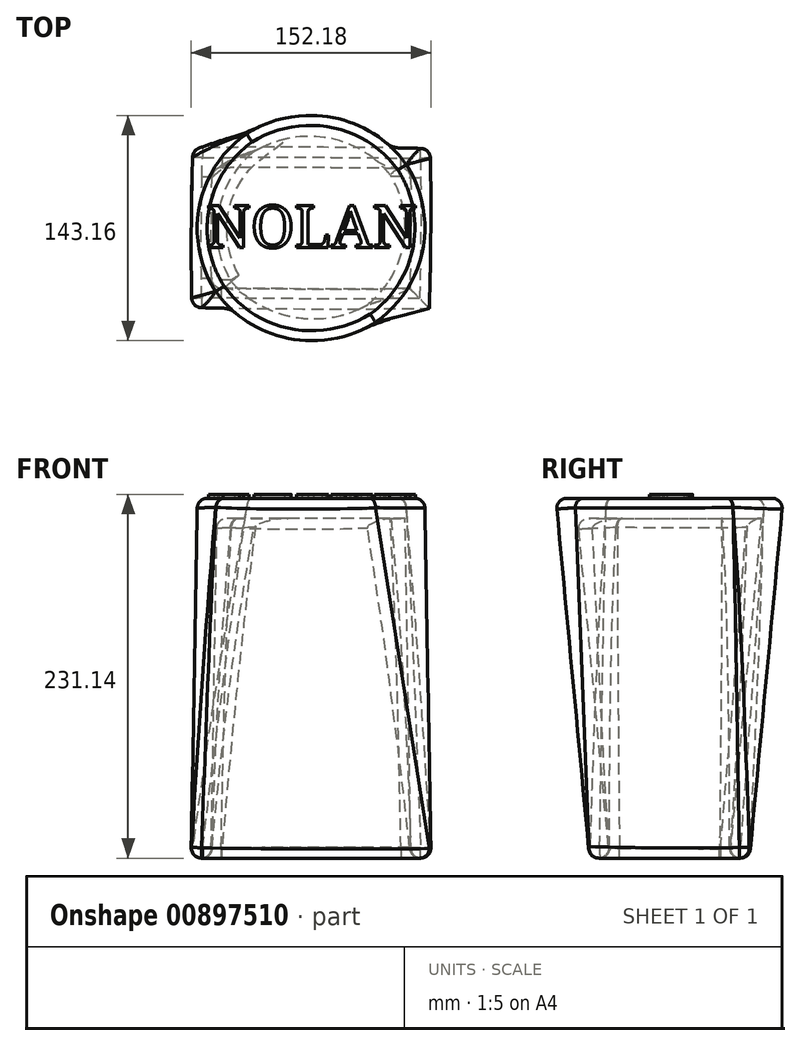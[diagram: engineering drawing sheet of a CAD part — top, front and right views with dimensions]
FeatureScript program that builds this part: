
annotation { "Feature Type Name" : "Feature", "Feature Type Description" : "" }
export const myFeature = defineFeature(function(context is Context, id is Id, definition is map)
    precondition{}
    {
        {
            var Q0;
            Q0=qCreatedBy(makeId("Top.planeOp"),FACE);
            var sketch = newSketch(context, id + "F0", { "sketchPlane" : qUnion([Q0])});
            skLineSegment(sketch, "E0.bottom", {"start": v(-76.2, -50.8) * mm, "end": v(76.2, -50.8) * mm});
            skLineSegment(sketch, "E0.top", {"start": v(-76.2, 50.8) * mm, "end": v(76.2, 50.8) * mm});
            skLineSegment(sketch, "E0.left", {"start": v(-76.2, -50.8) * mm, "end": v(-76.2, 50.8) * mm});
            skLineSegment(sketch, "E0.right", {"start": v(76.2, -50.8) * mm, "end": v(76.2, 50.8) * mm});
            skPoint(sketch, "E0.middle", {"position": v(0, 0) * mm});
            skSolve(sketch);
        }
        {
            var Q0;
            Q0=qCreatedBy(makeId("Top.planeOp"),FACE);
            cPlane(context, id + "F1", {"entities" : qUnion([Q0]), "cplaneType" : CPlaneType.OFFSET, "offset" : 228.6 * mm, "width" : 152.4 * mm, "height" : 152.4 * mm});
        }
        {
            var Q0;
            Q0=qCreatedBy(id+"F1.planeOp",FACE);
            var sketch = newSketch(context, id + "F2", { "sketchPlane" : qUnion([Q0])});
            skCircle(sketch, "E1", {"center": v(0, 0) * mm, "radius": 72.2 * mm});
            skSolve(sketch);
        }
        {
            var Q0;
            Q0=makeQuery(id+"F0.imprint","IMPRINT",FACE,{"disambiguationData":[TD([[makeQuery(id+"F0.imprint","IMPRINT",EDGE,{"derivedFrom":sQuery(id+"F0.wireOp",EDGE,"E0.bottom")}),1.0]])]});
            var Q1;
            Q1=makeQuery(id+"F2.imprint","IMPRINT",FACE,{"disambiguationData":[TD([[makeQuery(id+"F2.imprint","IMPRINT",EDGE,{"derivedFrom":sQuery(id+"F2.wireOp",EDGE,"E1")}),1.0]])]});
            loft(context, id + "F3", {"sheetProfilesArray" : [{ "sheetProfileEntities" : qUnion([Q0]) }, { "sheetProfileEntities" : qUnion([Q1]) }]});
        }
        {
            var Q0;
            Q0=makeQuery(id+"F3.opLoft","CAP_FACE",FACE,{"disambiguationData":[OSD([makeQuery(id+"F0.imprint","IMPRINT",FACE,{"disambiguationData":[TD([[makeQuery(id+"F0.imprint","IMPRINT",EDGE,{"derivedFrom":sQuery(id+"F0.wireOp",EDGE,"E0.bottom")}),1.0]])]})])],"isStart":true});
            shell(context, id + "F4", {"entities" : qUnion([Q0]), "thickness" : 12.7 * mm});
        }
        {
            var Q0;
            Q0=makeQuery(id+"F3.opLoft","SWEPT_EDGE",EDGE,{"disambiguationData":[OSD([sQuery(id+"F0.wireOp",EDGE,"E0.bottom"),sQuery(id+"F0.wireOp",EDGE,"E0.left")])]});
            var Q1;
            Q1=makeQuery(id+"F3.opLoft","MID_CAP_EDGE",EDGE,{"disambiguationData":[OSD([sQuery(id+"F0.wireOp",EDGE,"E0.bottom"),sQuery(id+"F0.wireOp",EDGE,"E0.left"),sQuery(id+"F0.wireOp",EDGE,"E0.right")])],"capPos":0.0});
            var Q2;
            Q2=makeQuery(id+"F3.opLoft","MID_CAP_EDGE",EDGE,{"disambiguationData":[OSD([sQuery(id+"F0.wireOp",EDGE,"E0.bottom"),sQuery(id+"F0.wireOp",EDGE,"E0.top"),sQuery(id+"F0.wireOp",EDGE,"E0.left")])],"capPos":0.0});
            var Q3;
            Q3=makeQuery(id+"F3.opLoft","MID_CAP_EDGE",EDGE,{"disambiguationData":[OSD([sQuery(id+"F0.wireOp",EDGE,"E0.bottom"),sQuery(id+"F0.wireOp",EDGE,"E0.top"),sQuery(id+"F0.wireOp",EDGE,"E0.left"),sQuery(id+"F0.wireOp",EDGE,"E0.right"),sQuery(id+"F2.wireOp",EDGE,"E1")])],"capPos":1.0});
            var Q4;
            Q4=makeQuery(id+"F3.opLoft","MID_CAP_EDGE",EDGE,{"disambiguationData":[OSD([sQuery(id+"F0.wireOp",EDGE,"E0.bottom"),sQuery(id+"F0.wireOp",EDGE,"E0.left"),sQuery(id+"F2.wireOp",EDGE,"E1")])],"capPos":1.0});
            var Q5;
            Q5=makeQuery(id+"F3.opLoft","MID_CAP_EDGE",EDGE,{"disambiguationData":[OSD([sQuery(id+"F0.wireOp",EDGE,"E0.bottom"),sQuery(id+"F0.wireOp",EDGE,"E0.top"),sQuery(id+"F0.wireOp",EDGE,"E0.right")])],"capPos":0.0});
            var Q6;
            Q6=makeQuery(id+"F3.opLoft","MID_CAP_EDGE",EDGE,{"disambiguationData":[OSD([sQuery(id+"F0.wireOp",EDGE,"E0.top"),sQuery(id+"F0.wireOp",EDGE,"E0.left"),sQuery(id+"F0.wireOp",EDGE,"E0.right")])],"capPos":0.0});
            var Q7;
            Q7=makeQuery(id+"F3.opLoft","SWEPT_EDGE",EDGE,{"disambiguationData":[OSD([sQuery(id+"F0.wireOp",EDGE,"E0.top"),sQuery(id+"F0.wireOp",EDGE,"E0.left"),sQuery(id+"F0.wireOp",EDGE,"E0.right"),sQuery(id+"F2.wireOp",EDGE,"E1")])]});
            var Q8;
            Q8=makeQuery(id+"F3.opLoft","MID_CAP_EDGE",EDGE,{"disambiguationData":[OSD([sQuery(id+"F0.wireOp",EDGE,"E0.bottom"),sQuery(id+"F0.wireOp",EDGE,"E0.top"),sQuery(id+"F0.wireOp",EDGE,"E0.right"),sQuery(id+"F2.wireOp",EDGE,"E1")])],"capPos":1.0});
            var Q9;
            Q9=makeQuery(id+"F4.opShell","OFFSET_EDGE",EDGE,{"disambiguationData":[OSD([sQuery(id+"F0.wireOp",EDGE,"E0.bottom"),sQuery(id+"F0.wireOp",EDGE,"E0.left"),sQuery(id+"F0.wireOp",EDGE,"E0.right")])]});
            var Q10;
            Q10=makeQuery(id+"F4.opShell","OFFSET_EDGE",EDGE,{"disambiguationData":[OSD([sQuery(id+"F0.wireOp",EDGE,"E0.bottom"),sQuery(id+"F0.wireOp",EDGE,"E0.top"),sQuery(id+"F0.wireOp",EDGE,"E0.left")])]});
            var Q11;
            Q11=makeQuery(id+"F4.opShell","OFFSET_EDGE",EDGE,{"disambiguationData":[OSD([sQuery(id+"F0.wireOp",EDGE,"E0.bottom"),sQuery(id+"F0.wireOp",EDGE,"E0.top"),sQuery(id+"F0.wireOp",EDGE,"E0.right")])]});
            var Q12;
            Q12=makeQuery(id+"F4.opShell","OFFSET_EDGE",EDGE,{"disambiguationData":[OSD([sQuery(id+"F0.wireOp",EDGE,"E0.top"),sQuery(id+"F0.wireOp",EDGE,"E0.left"),sQuery(id+"F0.wireOp",EDGE,"E0.right")])]});
            var Q13;
            Q13=makeQuery(id+"F3.opLoft","SWEPT_EDGE",EDGE,{"disambiguationData":[OSD([sQuery(id+"F0.wireOp",EDGE,"E0.bottom"),sQuery(id+"F0.wireOp",EDGE,"E0.left"),sQuery(id+"F0.wireOp",EDGE,"E0.right"),sQuery(id+"F2.wireOp",EDGE,"E1")])]});
            var Q14;
            Q14=makeQuery(id+"F3.opLoft","MID_CAP_EDGE",EDGE,{"disambiguationData":[OSD([sQuery(id+"F0.wireOp",EDGE,"E0.bottom"),sQuery(id+"F0.wireOp",EDGE,"E0.left"),sQuery(id+"F0.wireOp",EDGE,"E0.right"),sQuery(id+"F2.wireOp",EDGE,"E1")])],"capPos":1.0});
            var Q15;
            Q15=makeQuery(id+"F3.opLoft","SWEPT_EDGE",EDGE,{"disambiguationData":[OSD([sQuery(id+"F0.wireOp",EDGE,"E0.bottom"),sQuery(id+"F0.wireOp",EDGE,"E0.top"),sQuery(id+"F0.wireOp",EDGE,"E0.right"),sQuery(id+"F2.wireOp",EDGE,"E1")])]});
            var Q16;
            Q16=makeQuery(id+"F4.opShell","OFFSET_EDGE",EDGE,{"disambiguationData":[OSD([sQuery(id+"F0.wireOp",EDGE,"E0.bottom"),sQuery(id+"F0.wireOp",EDGE,"E0.left")])]});
            var Q17;
            Q17=makeQuery(id+"F4.opShell","OFFSET_EDGE",EDGE,{"disambiguationData":[OSD([sQuery(id+"F0.wireOp",EDGE,"E0.bottom"),sQuery(id+"F0.wireOp",EDGE,"E0.top"),sQuery(id+"F0.wireOp",EDGE,"E0.left"),sQuery(id+"F0.wireOp",EDGE,"E0.right"),sQuery(id+"F2.wireOp",EDGE,"E1")])]});
            var Q18;
            Q18=makeQuery(id+"F4.opShell","OFFSET_EDGE",EDGE,{"disambiguationData":[OSD([sQuery(id+"F0.wireOp",EDGE,"E0.bottom"),sQuery(id+"F0.wireOp",EDGE,"E0.left"),sQuery(id+"F2.wireOp",EDGE,"E1")])]});
            var Q19;
            Q19=makeQuery(id+"F4.opShell","OFFSET_EDGE",EDGE,{"disambiguationData":[OSD([sQuery(id+"F0.wireOp",EDGE,"E0.top"),sQuery(id+"F0.wireOp",EDGE,"E0.left"),sQuery(id+"F0.wireOp",EDGE,"E0.right"),sQuery(id+"F2.wireOp",EDGE,"E1")])]});
            var Q20;
            {var subQ0=sQuery(id+"F2.wireOp",EDGE,"E1");var subQ1=sQuery(id+"F0.wireOp",EDGE,"E0.right");var subQ2=sQuery(id+"F0.wireOp",EDGE,"E0.left");var subQ3=sQuery(id+"F0.wireOp",EDGE,"E0.bottom");Q20=makeQuery(id+"F4.opShell","OFFSET_EDGE",EDGE,{"disambiguationData":[OSD([subQ3,subQ2,subQ1,subQ0]),TDD([makeQuery(id+"F3.opLoft","SWEPT_EDGE",EDGE,{"disambiguationData":[OSD([subQ3,subQ2,subQ1,subQ0])]})])]});}
            var Q21;
            {var subQ0=sQuery(id+"F2.wireOp",EDGE,"E1");var subQ1=sQuery(id+"F0.wireOp",EDGE,"E0.right");var subQ2=sQuery(id+"F0.wireOp",EDGE,"E0.left");var subQ3=sQuery(id+"F0.wireOp",EDGE,"E0.bottom");Q21=makeQuery(id+"F4.opShell","OFFSET_EDGE",EDGE,{"disambiguationData":[OSD([subQ3,subQ2,subQ1,subQ0]),TDD([makeQuery(id+"F3.opLoft","MID_CAP_EDGE",EDGE,{"disambiguationData":[OSD([subQ3,subQ2,subQ1,subQ0])],"capPos":1.0})])]});}
            var Q22;
            {var subQ0=sQuery(id+"F2.wireOp",EDGE,"E1");var subQ1=sQuery(id+"F0.wireOp",EDGE,"E0.right");var subQ2=sQuery(id+"F0.wireOp",EDGE,"E0.top");var subQ3=sQuery(id+"F0.wireOp",EDGE,"E0.bottom");Q22=makeQuery(id+"F4.opShell","OFFSET_EDGE",EDGE,{"disambiguationData":[OSD([subQ3,subQ2,subQ1,subQ0]),TDD([makeQuery(id+"F3.opLoft","SWEPT_EDGE",EDGE,{"disambiguationData":[OSD([subQ3,subQ2,subQ1,subQ0])]})])]});}
            var Q23;
            {var subQ0=sQuery(id+"F2.wireOp",EDGE,"E1");var subQ1=sQuery(id+"F0.wireOp",EDGE,"E0.right");var subQ2=sQuery(id+"F0.wireOp",EDGE,"E0.top");var subQ3=sQuery(id+"F0.wireOp",EDGE,"E0.bottom");Q23=makeQuery(id+"F4.opShell","OFFSET_EDGE",EDGE,{"disambiguationData":[OSD([subQ3,subQ2,subQ1,subQ0]),TDD([makeQuery(id+"F3.opLoft","MID_CAP_EDGE",EDGE,{"disambiguationData":[OSD([subQ3,subQ2,subQ1,subQ0])],"capPos":1.0})])]});}
            fillet(context, id + "F5", {"entities" : qUnion([Q0, Q1, Q2, Q3, Q4, Q5, Q6, Q7, Q8, Q9, Q10, Q11, Q12, Q13, Q14, Q15, Q16, Q17, Q18, Q19, Q20, Q21, Q22, Q23]), "radius" : 6.35 * mm, "tangentPropagation" : true, "allowEdgeOverflow" : false});
        }
        {
            var Q0;
            Q0=makeQuery(id+"F3.opLoft","CAP_FACE",FACE,{"disambiguationData":[OSD([makeQuery(id+"F2.imprint","IMPRINT",FACE,{"disambiguationData":[TD([[makeQuery(id+"F2.imprint","IMPRINT",EDGE,{"derivedFrom":sQuery(id+"F2.wireOp",EDGE,"E1")}),1.0]])]})])],"isStart":true});
            var sketch = newSketch(context, id + "F6", { "sketchPlane" : qUnion([Q0])});
            skText(sketch, "E2", { "text": "NOLAN", "fontName": "NotoSerif-Regular.ttf"});
            const initialGuessF6  = {"E2": [-0.0666, -0.0124, 1, 0, 0.02681]};
            skSetInitialGuess(sketch, initialGuessF6);
            skSolve(sketch);
        }
        {
            var Q0;
            Q0 = qSketchRegion(id + "F6", true);
            extrude(context, id + "F7", {"entities" : qUnion([Q0]), "operationType" : NewBodyOperationType.ADD, "depth" : 2.54 * mm, "offsetDistance" : 25.4 * mm});
        }
    });
